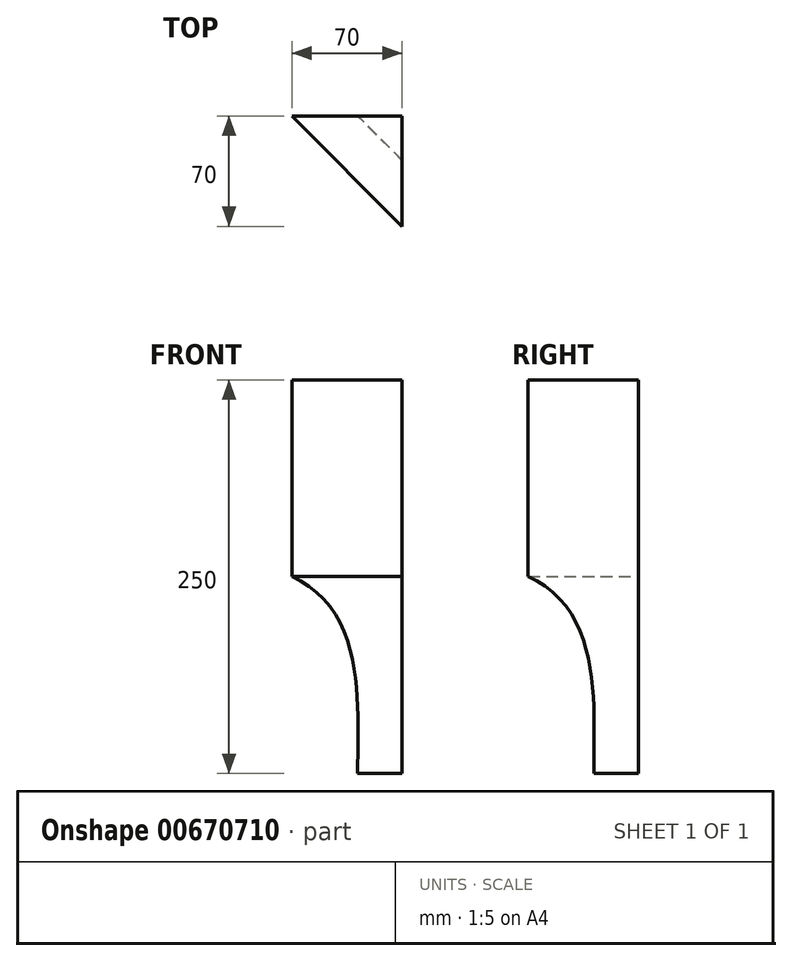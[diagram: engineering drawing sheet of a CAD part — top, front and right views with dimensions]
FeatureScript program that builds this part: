
annotation { "Feature Type Name" : "Feature", "Feature Type Description" : "" }
export const myFeature = defineFeature(function(context is Context, id is Id, definition is map)
    precondition{}
    {
        {
            var Q0;
            Q0=qCreatedBy(makeId("Top.planeOp"),FACE);
            var sketch = newSketch(context, id + "F0", { "sketchPlane" : qUnion([Q0])});
            skLineSegment(sketch, "E0.bottom", {"start": v(-35.18, 36.42) * mm, "end": v(34.82, 36.42) * mm});
            skLineSegment(sketch, "E0.right", {"start": v(34.82, 36.42) * mm, "end": v(34.82, -33.58) * mm});
            skLineSegment(sketch, "E1", {"start": v(-35.18, 36.42) * mm, "end": v(34.82, -33.58) * mm});
            skSolve(sketch);
        }
        {
            var Q0;
            Q0 = qSketchRegion(id + "F0", true);
            extrude(context, id + "F1", {"entities" : qUnion([Q0]), "depth" : 250 * mm, "offsetDistance" : 25 * mm});
        }
        {
            var Q0;
            Q0=makeQuery(id+"F1.opExtrude","CAP_EDGE",EDGE,{"disambiguationData":[OSD([sQuery(id+"F0.wireOp",EDGE,"E1")])],"isStart":false});
            cPoint(context, id + "F2", {"entities" : qUnion([Q0]), "parameter" : 0.5});
        }
        {
            var Q0;
            Q0=makeQuery(id+"F1.opExtrude","CAP_VERTEX",VERTEX,{"disambiguationData":[OSD([sQuery(id+"F0.wireOp",EDGE,"E0.bottom"),sQuery(id+"F0.wireOp",EDGE,"E0.right")])],"isStart":true});
            var Q1;
            Q1=makeQuery(id+"F1.opExtrude","CAP_VERTEX",VERTEX,{"disambiguationData":[OSD([sQuery(id+"F0.wireOp",EDGE,"E0.bottom"),sQuery(id+"F0.wireOp",EDGE,"E0.right")])],"isStart":false});
            var Q2;
            Q2 = qCreatedBy(id + "F2" ,VERTEX);
            cPlane(context, id + "F3", {"entities" : qUnion([Q0, Q1, Q2]), "cplaneType" : CPlaneType.THREE_POINT, "offset" : 25 * mm, "width" : 150 * mm, "height" : 150 * mm});
        }
        {
            var Q0;
            Q0=qCreatedBy(id+"F3.planeOp",FACE);
            var sketch = newSketch(context, id + "F4", { "sketchPlane" : qUnion([Q0])});
            skFitSpline(sketch, "E2", {"points": [v(-30.38, 0) * mm, v(-0.88, 125) * mm, v(47.73, 0) * mm], "startDerivative": vector(-0.32, 270.98) * mm, "endDerivative": vector(-348.3, -769.9) * mm});
            skLineSegment(sketch, "E3", {"start": v(-30.38, 0) * mm, "end": v(47.73, 0) * mm});
            skSolve(sketch);
        }
        {
            var Q0;
            Q0=makeQuery(id+"F4.imprint","IMPRINT",FACE,{"disambiguationData":[TD([[makeQuery(id+"F4.imprint","IMPRINT",EDGE,{"derivedFrom":sQuery(id+"F4.wireOp",EDGE,"E2")}),-1.0]])]});
            extrude(context, id + "F5", {"entities" : qUnion([Q0]), "operationType" : NewBodyOperationType.REMOVE, "endBound" : BoundingType.THROUGH_ALL, "oppositeDirection" : true, "depth" : 25 * mm, "offsetDistance" : 25 * mm, "hasSecondDirection" : true, "secondDirectionBound" : SecondDirectionBoundingType.THROUGH_ALL, "secondDirectionOppositeDirection" : false, "secondDirectionDepth" : 25 * mm});
        }
    });
